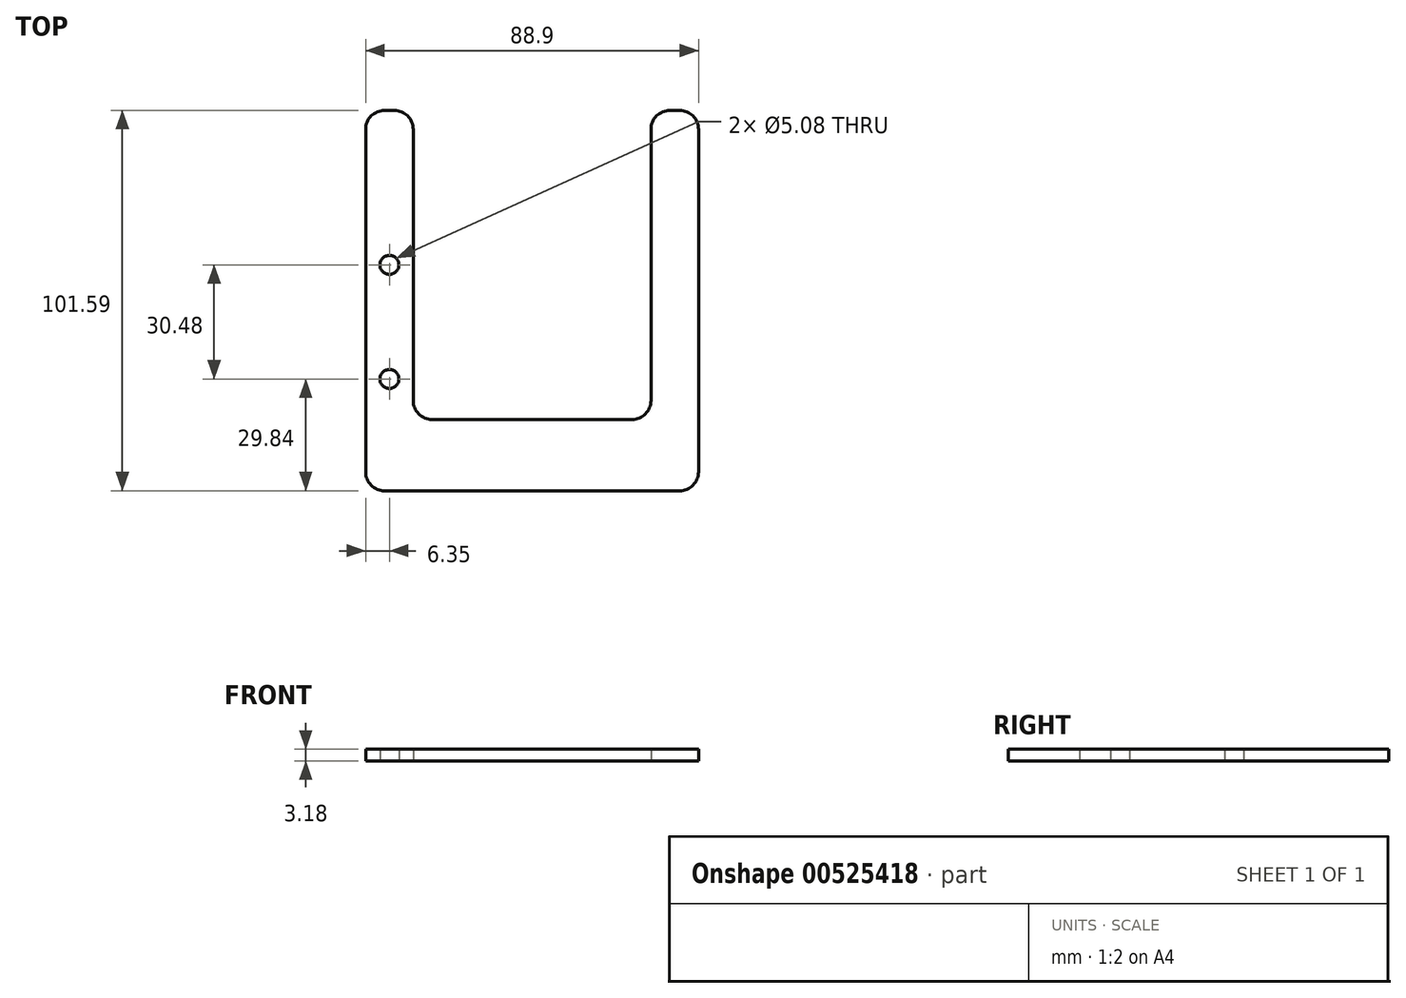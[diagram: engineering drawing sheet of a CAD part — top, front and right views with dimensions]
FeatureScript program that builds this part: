
annotation { "Feature Type Name" : "Feature", "Feature Type Description" : "" }
export const myFeature = defineFeature(function(context is Context, id is Id, definition is map)
    precondition{}
    {
        {
            var Q0;
            Q0=qCreatedBy(makeId("Top.planeOp"),FACE);
            var sketch = newSketch(context, id + "F0", { "sketchPlane" : qUnion([Q0])});
            skLineSegment(sketch, "E0.bottom", {"start": v(-71.12, 71.75) * mm, "end": v(-68.58, 71.75) * mm});
            skLineSegment(sketch, "E0.left", {"start": v(-76.2, 66.67) * mm, "end": v(-76.2, -10.8) * mm});
            skLineSegment(sketch, "E0.right", {"start": v(-63.5, 66.68) * mm, "end": v(-63.5, -5.72) * mm});
            skLineSegment(sketch, "E1.bottom", {"start": v(-58.42, -10.8) * mm, "end": v(-5.08, -10.8) * mm});
            skLineSegment(sketch, "E1.top", {"start": v(-71.12, -29.85) * mm, "end": v(7.62, -29.84) * mm});
            skLineSegment(sketch, "E1.left", {"start": v(-76.2, -10.8) * mm, "end": v(-76.2, -24.77) * mm});
            skLineSegment(sketch, "E1.right", {"start": v(12.7, -10.8) * mm, "end": v(12.7, -24.76) * mm});
            skLineSegment(sketch, "E2.top", {"start": v(7.62, 71.76) * mm, "end": v(5.08, 71.76) * mm});
            skLineSegment(sketch, "E2.left", {"start": v(12.7, -10.8) * mm, "end": v(12.7, 66.68) * mm});
            skLineSegment(sketch, "E2.right", {"start": v(0, -5.71) * mm, "end": v(0, 66.68) * mm});
            skCircle(sketch, "E3", {"center": v(-69.85, 30.48) * mm, "radius": 2.54 * mm});
            skPoint(sketch, "E3.centerSnap0", {"position": v(-63.5, 30.48) * mm});
            skPoint(sketch, "E3.centerSnap1", {"position": v(-69.85, 71.76) * mm});
            skCircle(sketch, "E4", {"center": v(-69.85, 0) * mm, "radius": 2.54 * mm});
            skPoint(sketch, "E5.visualSharp", {"position": v(-63.5, 71.75) * mm});
            skArc(sketch, "E5.filletArc", {"start": v(-63.5, 66.68) * mm, "mid": v(-64.99, 70.27) * mm, "end": v(-68.58, 71.76) * mm});
            skPoint(sketch, "E6.visualSharp", {"position": v(-63.5, -10.8) * mm});
            skArc(sketch, "E6.filletArc", {"start": v(-63.5, -5.72) * mm, "mid": v(-62.01, -9.3) * mm, "end": v(-58.42, -10.8) * mm});
            skPoint(sketch, "E7.visualSharp", {"position": v(0, -10.8) * mm});
            skArc(sketch, "E7.filletArc", {"start": v(-5.08, -10.8) * mm, "mid": v(-1.49, -9.3) * mm, "end": v(0, -5.71) * mm});
            skPoint(sketch, "E8.visualSharp", {"position": v(12.7, -29.84) * mm});
            skArc(sketch, "E8.filletArc", {"start": v(7.62, -29.84) * mm, "mid": v(11.21, -28.36) * mm, "end": v(12.7, -24.76) * mm});
            skPoint(sketch, "E9.visualSharp", {"position": v(12.7, 71.76) * mm});
            skArc(sketch, "E9.filletArc", {"start": v(12.7, 66.68) * mm, "mid": v(11.21, 70.27) * mm, "end": v(7.62, 71.76) * mm});
            skPoint(sketch, "E10.visualSharp", {"position": v(0, 71.76) * mm});
            skArc(sketch, "E10.filletArc", {"start": v(5.08, 71.76) * mm, "mid": v(1.49, 70.27) * mm, "end": v(0, 66.68) * mm});
            skPoint(sketch, "E11.visualSharp", {"position": v(-76.2, 71.76) * mm});
            skArc(sketch, "E11.filletArc", {"start": v(-71.12, 71.76) * mm, "mid": v(-74.71, 70.27) * mm, "end": v(-76.2, 66.67) * mm});
            skPoint(sketch, "E12.visualSharp", {"position": v(-76.2, -29.85) * mm});
            skArc(sketch, "E12.filletArc", {"start": v(-76.2, -24.77) * mm, "mid": v(-74.71, -28.36) * mm, "end": v(-71.12, -29.85) * mm});
            skSolve(sketch);
        }
        {
            var Q0;
            Q0=makeQuery(id+"F0.imprint","IMPRINT",FACE,{"disambiguationData":[TD([[makeQuery(id+"F0.imprint","IMPRINT",EDGE,{"derivedFrom":sQuery(id+"F0.wireOp",EDGE,"E0.bottom")}),-1.0]])]});
            var sketch = newSketch(context, id + "F1", { "sketchPlane" : qUnion([Q0])});
            skSolve(sketch);
        }
        {
            var Q0;
            Q0 = qSketchRegion(id + "F1", true);
            var Q1;
            Q1=makeQuery(id+"F0.imprint","IMPRINT",FACE,{"disambiguationData":[TD([[makeQuery(id+"F0.imprint","IMPRINT",EDGE,{"derivedFrom":sQuery(id+"F0.wireOp",EDGE,"E0.bottom")}),-1.0]])]});
            extrude(context, id + "F2", {"entities" : qUnion([Q0, Q1]), "depth" : 3.17 * mm, "offsetDistance" : 25.4 * mm});
        }
    });
